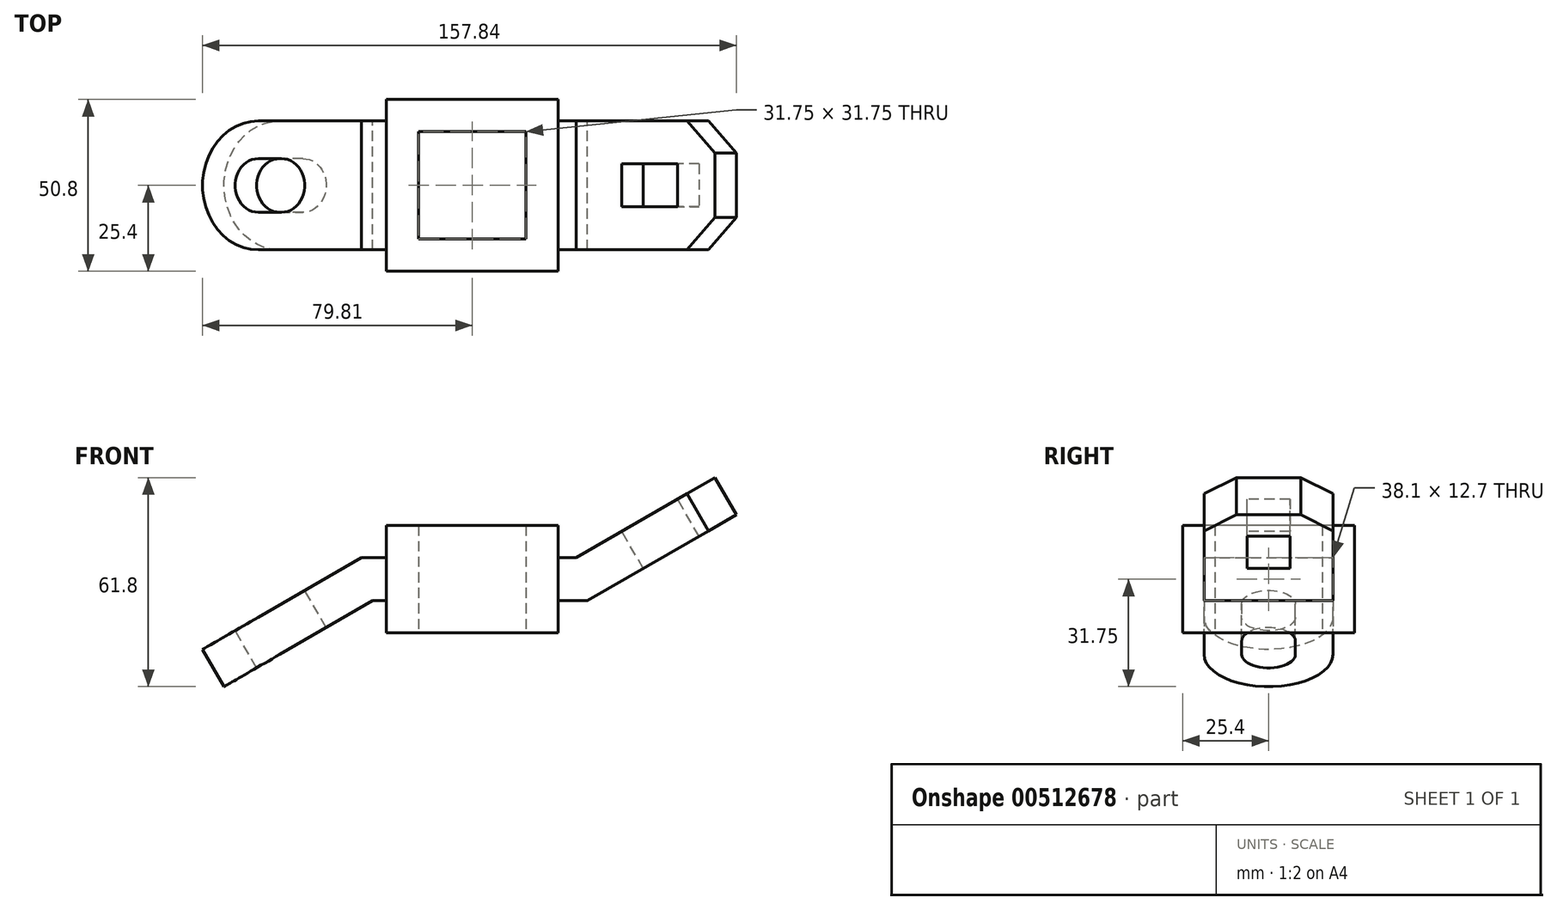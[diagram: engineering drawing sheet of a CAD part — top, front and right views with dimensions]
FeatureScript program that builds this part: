
annotation { "Feature Type Name" : "Feature", "Feature Type Description" : "" }
export const myFeature = defineFeature(function(context is Context, id is Id, definition is map)
    precondition{}
    {
        {
            var Q0;
            Q0=qCreatedBy(makeId("Top.planeOp"),FACE);
            var sketch = newSketch(context, id + "F0", { "sketchPlane" : qUnion([Q0])});
            skLineSegment(sketch, "E0.bottom", {"start": v(-25.4, 25.4) * mm, "end": v(25.4, 25.4) * mm});
            skLineSegment(sketch, "E0.top", {"start": v(-25.4, -25.4) * mm, "end": v(25.4, -25.4) * mm});
            skLineSegment(sketch, "E0.left", {"start": v(-25.4, 25.4) * mm, "end": v(-25.4, -25.4) * mm});
            skLineSegment(sketch, "E0.right", {"start": v(25.4, 25.4) * mm, "end": v(25.4, -25.4) * mm});
            skLineSegment(sketch, "E1.bottom", {"start": v(-15.88, 15.88) * mm, "end": v(15.88, 15.88) * mm});
            skLineSegment(sketch, "E1.top", {"start": v(-15.88, -15.88) * mm, "end": v(15.88, -15.88) * mm});
            skLineSegment(sketch, "E1.left", {"start": v(-15.88, 15.88) * mm, "end": v(-15.88, -15.88) * mm});
            skLineSegment(sketch, "E1.right", {"start": v(15.88, 15.88) * mm, "end": v(15.88, -15.88) * mm});
            skSolve(sketch);
        }
        {
            var Q0;
            Q0 = qSketchRegion(id + "F0", true);
            extrude(context, id + "F1", {"entities" : qUnion([Q0]), "endBound" : BoundingType.SYMMETRIC, "depth" : 31.75 * mm});
        }
        {
            var Q0;
            Q0=qCreatedBy(makeId("Front.planeOp"),FACE);
            var sketch = newSketch(context, id + "F2", { "sketchPlane" : qUnion([Q0])});
            skLineSegment(sketch, "E2", {"start": v(-29.47, -6.35) * mm, "end": v(34.03, -6.35) * mm});
            skLineSegment(sketch, "E3", {"start": v(-29.47, -6.35) * mm, "end": v(-73.46, -31.75) * mm});
            skLineSegment(sketch, "E4", {"start": v(-73.46, -31.75) * mm, "end": v(-79.81, -20.75) * mm});
            skLineSegment(sketch, "E5", {"start": v(-79.81, -20.75) * mm, "end": v(-32.87, 6.35) * mm});
            skPoint(sketch, "E6.orphan", {"position": v(-35.72, 6.35) * mm});
            skPoint(sketch, "E7.orphan", {"position": v(-35.33, -6.35) * mm});
            skLineSegment(sketch, "E8", {"start": v(34.03, -6.35) * mm, "end": v(78.03, 19.05) * mm});
            skLineSegment(sketch, "E9", {"start": v(78.03, 19.05) * mm, "end": v(71.68, 30.05) * mm});
            skLineSegment(sketch, "E10", {"start": v(71.68, 30.05) * mm, "end": v(30.63, 6.35) * mm});
            skLineSegment(sketch, "E11.trimOffspring", {"start": v(30.63, 6.35) * mm, "end": v(-32.87, 6.35) * mm});
            skSolve(sketch);
        }
        {
            var Q0;
            Q0 = qSketchRegion(id + "F2", true);
            extrude(context, id + "F3", {"entities" : qUnion([Q0]), "operationType" : NewBodyOperationType.ADD, "endBound" : BoundingType.SYMMETRIC, "depth" : 38.1 * mm});
        }
        {
            var Q0;
            Q0=makeQuery(id+"F3.opExtrude","SWEPT_FACE",FACE,{"disambiguationData":[OSD([sQuery(id+"F2.wireOp",EDGE,"E5")])]});
            var sketch = newSketch(context, id + "F4", { "sketchPlane" : qUnion([Q0])});
            skLineSegment(sketch, "E12", {"start": v(-87.17, 0) * mm, "end": v(-68.38, 0) * mm});
            skArc(sketch, "E13", {"start": v(-60.45, 7.94) * mm, "mid": v(-68.38, 0) * mm, "end": v(-60.45, -7.94) * mm});
            skArc(sketch, "E14", {"start": v(-52.5, -7.94) * mm, "mid": v(-44.57, 0) * mm, "end": v(-52.5, 7.94) * mm});
            skLineSegment(sketch, "E15", {"start": v(-60.45, 7.94) * mm, "end": v(-52.5, 7.94) * mm});
            skLineSegment(sketch, "E16", {"start": v(-52.5, -7.94) * mm, "end": v(-60.45, -7.94) * mm});
            skArc(sketch, "E17", {"start": v(-60.45, 19.05) * mm, "mid": v(-79.5, 0) * mm, "end": v(-60.45, -19.05) * mm});
            skSolve(sketch);
        }
        {
            var Q0;
            Q0 = qSketchRegion(id + "F4", true);
            extrude(context, id + "F5", {"entities" : qUnion([Q0]), "operationType" : NewBodyOperationType.REMOVE, "oppositeDirection" : true, "depth" : 25.4 * mm});
        }
        {
            var Q0;
            Q0=makeQuery(id+"F3.opExtrude","CAP_EDGE",EDGE,{"disambiguationData":[OSD([sQuery(id+"F2.wireOp",EDGE,"E4")])],"isStart":false});
            var Q1;
            Q1=makeQuery(id+"F3.opExtrude","CAP_EDGE",EDGE,{"disambiguationData":[OSD([sQuery(id+"F2.wireOp",EDGE,"E4")])],"isStart":true});
            fillet(context, id + "F6", {"entities" : qUnion([Q0, Q1]), "radius" : 19.05 * mm, "tangentPropagation" : true, "allowEdgeOverflow" : false});
        }
        {
            var Q0;
            Q0=makeQuery(id+"F3.opExtrude","SWEPT_FACE",FACE,{"disambiguationData":[OSD([sQuery(id+"F2.wireOp",EDGE,"E10")])]});
            var sketch = newSketch(context, id + "F7", { "sketchPlane" : qUnion([Q0])});
            skLineSegment(sketch, "E18", {"start": v(45.35, 6.35) * mm, "end": v(45.35, -6.35) * mm});
            skLineSegment(sketch, "E19", {"start": v(64.4, 6.35) * mm, "end": v(64.4, -6.35) * mm});
            skLineSegment(sketch, "E20", {"start": v(64.4, 6.35) * mm, "end": v(45.35, 6.35) * mm});
            skLineSegment(sketch, "E21", {"start": v(45.35, -6.35) * mm, "end": v(64.4, -6.35) * mm});
            skSolve(sketch);
        }
        {
            var Q0;
            Q0 = qSketchRegion(id + "F7", true);
            extrude(context, id + "F8", {"entities" : qUnion([Q0]), "operationType" : NewBodyOperationType.REMOVE, "endBound" : BoundingType.THROUGH_ALL, "oppositeDirection" : true, "depth" : 25.4 * mm});
        }
        {
            var Q0;
            Q0=makeQuery(id+"F3.opExtrude","CAP_EDGE",EDGE,{"disambiguationData":[OSD([sQuery(id+"F2.wireOp",EDGE,"E9")])],"isStart":true});
            var Q1;
            Q1=makeQuery(id+"F3.opExtrude","CAP_EDGE",EDGE,{"disambiguationData":[OSD([sQuery(id+"F2.wireOp",EDGE,"E9")])],"isStart":false});
            chamfer(context, id + "F9", {"entities" : qUnion([Q0, Q1]), "width" : 9.52 * mm, "tangentPropagation" : true});
        }
        {
            var Q0;
            Q0=makeQuery(id+"F3.boolean.opBoolean","SPLIT",FACE,{"disambiguationData":[TD([makeQuery(id+"F1.opExtrude","SWEPT_FACE",FACE,{"disambiguationData":[OSD([sQuery(id+"F0.wireOp",EDGE,"E1.bottom")])]})])],"derivedFrom":makeQuery(id+"F3.opExtrude","SWEPT_FACE",FACE,{"disambiguationData":[OSD([sQuery(id+"F2.wireOp",EDGE,"E11.trimOffspring")])]})});
            extrude(context, id + "F10", {"entities" : qUnion([Q0]), "operationType" : NewBodyOperationType.REMOVE, "endBound" : BoundingType.THROUGH_ALL, "oppositeDirection" : true, "depth" : 25.4 * mm});
        }
    });
